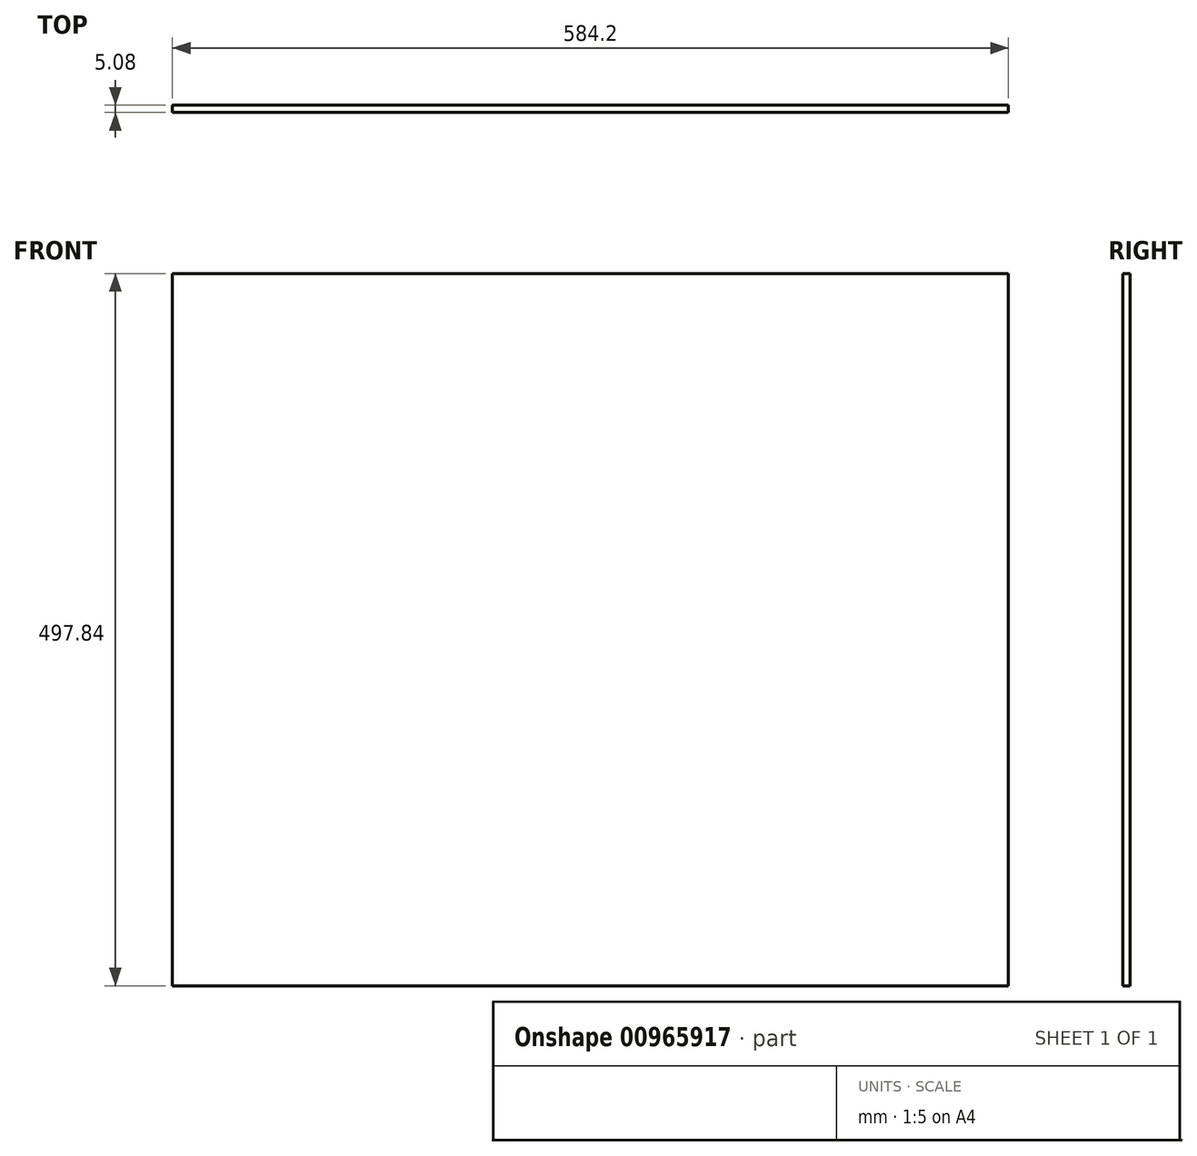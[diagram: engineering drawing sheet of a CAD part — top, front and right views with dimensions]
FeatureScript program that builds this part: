
annotation { "Feature Type Name" : "Feature", "Feature Type Description" : "" }
export const myFeature = defineFeature(function(context is Context, id is Id, definition is map)
    precondition{}
    {
        {
            var Q0;
            Q0=qCreatedBy(makeId("Front.planeOp"),FACE);
            var sketch = newSketch(context, id + "F0", { "sketchPlane" : qUnion([Q0])});
            skLineSegment(sketch, "E0.bottom", {"start": v(-293.71, 232.15) * mm, "end": v(290.49, 232.15) * mm});
            skLineSegment(sketch, "E0.top", {"start": v(-293.71, -265.69) * mm, "end": v(290.49, -265.69) * mm});
            skLineSegment(sketch, "E0.left", {"start": v(-293.71, 232.15) * mm, "end": v(-293.71, -265.69) * mm});
            skLineSegment(sketch, "E0.right", {"start": v(290.49, 232.15) * mm, "end": v(290.49, -265.69) * mm});
            skSolve(sketch);
        }
        {
            var Q0;
            Q0=makeQuery(id+"F0.imprint","IMPRINT",FACE,{"disambiguationData":[TD([[makeQuery(id+"F0.imprint","IMPRINT",EDGE,{"derivedFrom":sQuery(id+"F0.wireOp",EDGE,"E0.bottom")}),-1.0]])]});
            extrude(context, id + "F1", {"entities" : qUnion([Q0]), "depth" : 5.08 * mm, "offsetDistance" : 25.4 * mm});
        }
    });
